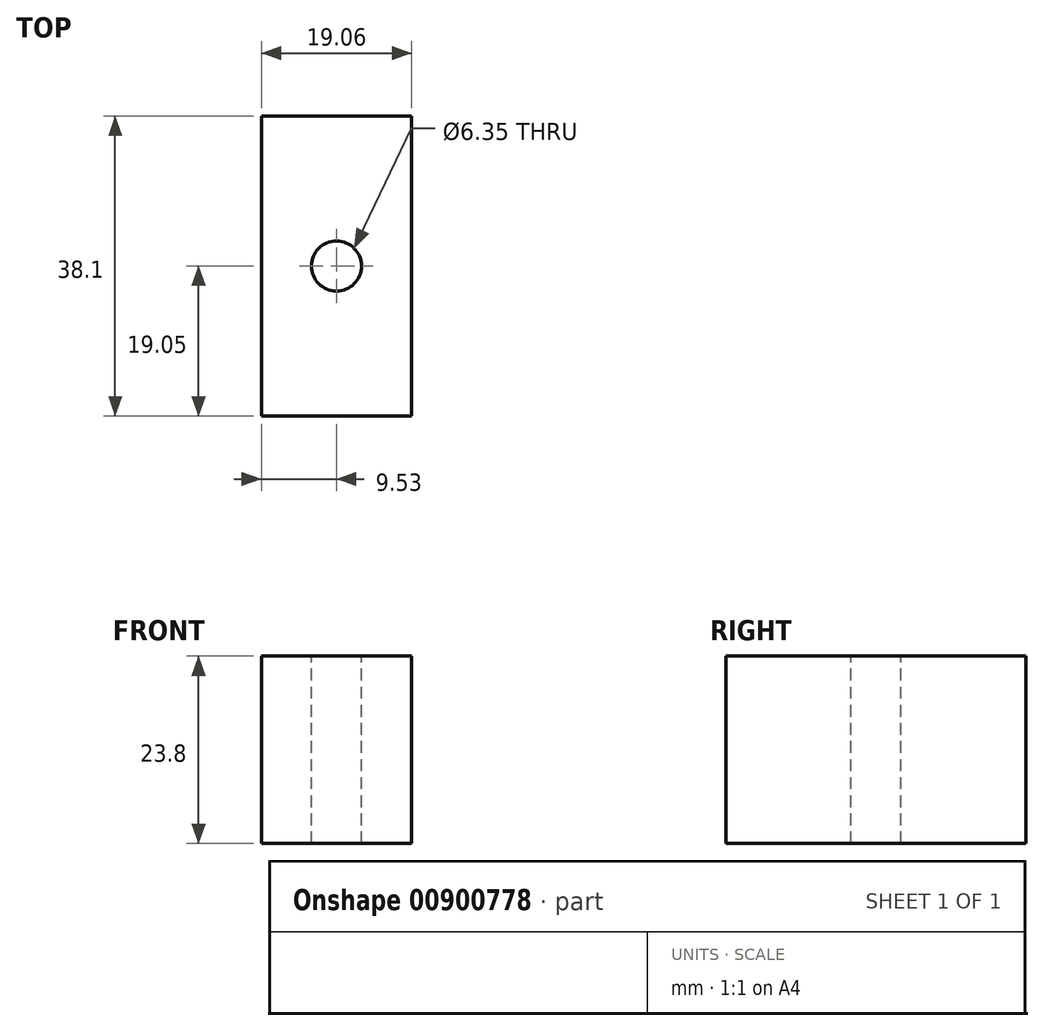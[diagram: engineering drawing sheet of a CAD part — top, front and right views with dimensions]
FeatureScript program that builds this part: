
annotation { "Feature Type Name" : "Feature", "Feature Type Description" : "" }
export const myFeature = defineFeature(function(context is Context, id is Id, definition is map)
    precondition{}
    {
        {
            var Q0;
            Q0=qCreatedBy(makeId("Front.planeOp"),FACE);
            var sketch = newSketch(context, id + "F0", { "sketchPlane" : qUnion([Q0])});
            skLineSegment(sketch, "E0.bottom", {"start": v(-9.53, 23.8) * mm, "end": v(9.52, 23.8) * mm});
            skLineSegment(sketch, "E0.top", {"start": v(-9.53, 0) * mm, "end": v(9.53, 0) * mm});
            skLineSegment(sketch, "E0.left", {"start": v(-9.53, 23.8) * mm, "end": v(-9.53, 0) * mm});
            skLineSegment(sketch, "E0.right", {"start": v(9.52, 23.8) * mm, "end": v(9.53, 0) * mm});
            skSolve(sketch);
        }
        {
            var Q0;
            Q0=makeQuery(id+"F0.imprint","IMPRINT",FACE,{"disambiguationData":[TD([[makeQuery(id+"F0.imprint","IMPRINT",EDGE,{"derivedFrom":sQuery(id+"F0.wireOp",EDGE,"E0.bottom")}),-1.0]])]});
            extrude(context, id + "F1", {"entities" : qUnion([Q0]), "depth" : 38.1 * mm, "offsetDistance" : 25.4 * mm});
        }
        {
            var Q0;
            Q0=makeQuery(id+"F1.opExtrude","SWEPT_FACE",FACE,{"disambiguationData":[OSD([sQuery(id+"F0.wireOp",EDGE,"E0.bottom")])]});
            var sketch = newSketch(context, id + "F2", { "sketchPlane" : qUnion([Q0])});
            skCircle(sketch, "E1", {"center": v(0, -19.05) * mm, "radius": 3.18 * mm});
            skSolve(sketch);
        }
        {
            var Q0;
            Q0=makeQuery(id+"F2.imprint","IMPRINT",FACE,{"disambiguationData":[TD([[makeQuery(id+"F2.imprint","IMPRINT",EDGE,{"derivedFrom":sQuery(id+"F2.wireOp",EDGE,"E1")}),1.0]])]});
            extrude(context, id + "F3", {"entities" : qUnion([Q0]), "operationType" : NewBodyOperationType.REMOVE, "endBound" : BoundingType.THROUGH_ALL, "oppositeDirection" : true, "depth" : 25.4 * mm, "offsetDistance" : 25.4 * mm});
        }
    });
